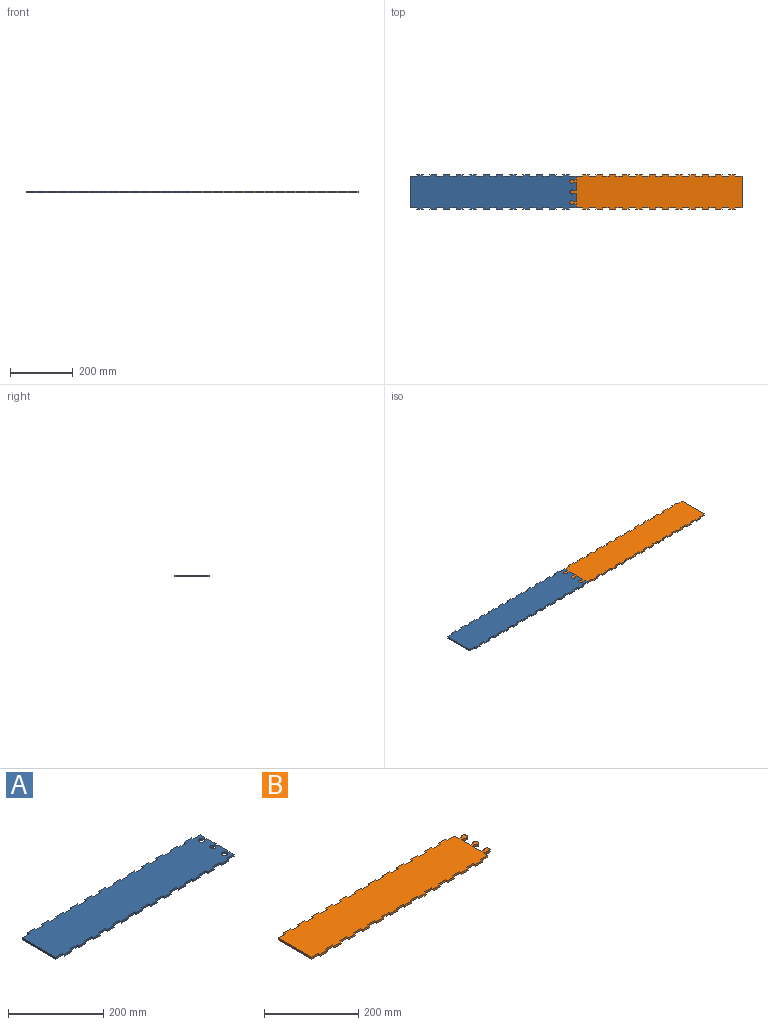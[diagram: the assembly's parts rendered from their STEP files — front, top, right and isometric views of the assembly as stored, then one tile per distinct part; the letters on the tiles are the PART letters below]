
ASSEMBLY  parts=2 mates=1
PART A: 114 faces, bbox 530x110x5.1 mm
  f0: plane 21.2x5.08mm, normal (0,1,0), area 107.7mm2, adj f1,f111,f112,f113
  f1: plane 5.08x5mm, normal (-1,0,0), area 25.4mm2, adj f0,f2,f112,f113
  f2: plane 21.2x5.08mm, normal (0,1,0), area 107.7mm2, adj f1,f3,f112,f113
  f3: plane 5.08x5mm, normal (1,0,0), area 25.4mm2, adj f2,f4,f112,f113
  f4: plane 21.2x5.08mm, normal (0,1,0), area 107.7mm2, adj f3,f5,f112,f113
  f5: plane 5.08x5mm, normal (-1,0,0), area 25.4mm2, adj f4,f6,f112,f113
  f6: plane 21.2x5.08mm, normal (0,1,0), area 107.7mm2, adj f5,f7,f112,f113
  f7: plane 5.08x5mm, normal (1,0,0), area 25.4mm2, adj f6,f8,f112,f113
  f8: plane 21.2x5.08mm, normal (0,1,0), area 107.7mm2, adj f7,f9,f112,f113
  f9: plane 5.08x5mm, normal (-1,0,0), area 25.4mm2, adj f8,f10,f112,f113
  f10: plane 21.2x5.08mm, normal (0,1,0), area 107.7mm2, adj f9,f11,f112,f113
  f11: plane 5.08x5mm, normal (1,0,0), area 25.4mm2, adj f10,f12,f112,f113
  f12: plane 21.2x5.08mm, normal (0,1,0), area 107.7mm2, adj f11,f13,f112,f113
  f13: plane 5.08x5mm, normal (-1,0,0), area 25.4mm2, adj f12,f14,f112,f113
  f14: plane 21.2x5.08mm, normal (0,1,0), area 107.7mm2, adj f13,f15,f112,f113
  f15: plane 5.08x5mm, normal (1,0,0), area 25.4mm2, adj f14,f16,f112,f113
  f16: plane 21.2x5.08mm, normal (0,1,0), area 107.7mm2, adj f15,f17,f112,f113
  f17: plane 5.08x5mm, normal (-1,0,0), area 25.4mm2, adj f16,f18,f112,f113
  f18: plane 21.2x5.08mm, normal (0,1,0), area 107.7mm2, adj f17,f19,f112,f113
  f19: plane 5.08x5mm, normal (1,0,0), area 25.4mm2, adj f18,f20,f112,f113
  f20: plane 21.2x5.08mm, normal (0,1,0), area 107.7mm2, adj f19,f21,f112,f113
  f21: plane 5.08x5mm, normal (-1,0,0), area 25.4mm2, adj f20,f22,f112,f113
  f22: plane 21.2x5.08mm, normal (0,1,0), area 107.7mm2, adj f21,f23,f112,f113
  f23: plane 100x5.08mm, normal (-1,0,0), area 508mm2, adj f22,f24,f112,f113
  f24: plane 21.2x5.08mm, normal (0,-1,0), area 107.7mm2, adj f23,f25,f112,f113
  f25: plane 5.08x5mm, normal (-1,0,0), area 25.4mm2, adj f24,f26,f112,f113
  f26: plane 21.2x5.08mm, normal (0,-1,0), area 107.7mm2, adj f25,f27,f112,f113
  f27: plane 5.08x5mm, normal (1,0,0), area 25.4mm2, adj f26,f28,f112,f113
  f28: plane 21.2x5.08mm, normal (0,-1,0), area 107.7mm2, adj f27,f29,f112,f113
  f29: plane 5.08x5mm, normal (-1,0,0), area 25.4mm2, adj f28,f30,f112,f113
  f30: plane 21.2x5.08mm, normal (0,-1,0), area 107.7mm2, adj f29,f31,f112,f113
  f31: plane 5.08x5mm, normal (1,0,0), area 25.4mm2, adj f30,f32,f112,f113
  f32: plane 21.2x5.08mm, normal (0,-1,0), area 107.7mm2, adj f31,f33,f112,f113
  f33: plane 5.08x5mm, normal (-1,0,0), area 25.4mm2, adj f32,f34,f112,f113
  f34: plane 21.2x5.08mm, normal (0,-1,0), area 107.7mm2, adj f33,f35,f112,f113
  f35: plane 5.08x5mm, normal (1,0,0), area 25.4mm2, adj f34,f36,f112,f113
  f36: plane 21.2x5.08mm, normal (0,-1,0), area 107.7mm2, adj f35,f37,f112,f113
  f37: plane 5.08x5mm, normal (-1,0,0), area 25.4mm2, adj f36,f38,f112,f113
  f38: plane 21.2x5.08mm, normal (0,-1,0), area 107.7mm2, adj f37,f39,f112,f113
  f39: plane 5.08x5mm, normal (1,0,0), area 25.4mm2, adj f38,f40,f112,f113
  f40: plane 21.2x5.08mm, normal (0,-1,0), area 107.7mm2, adj f39,f41,f112,f113
  f41: plane 5.08x5mm, normal (-1,0,0), area 25.4mm2, adj f40,f42,f112,f113
  f42: plane 21.2x5.08mm, normal (0,-1,0), area 107.7mm2, adj f41,f43,f112,f113
  f43: plane 5.08x5mm, normal (1,0,0), area 25.4mm2, adj f42,f44,f112,f113
  f44: plane 21.2x5.08mm, normal (0,-1,0), area 107.7mm2, adj f43,f45,f112,f113
  f45: plane 5.08x5mm, normal (-1,0,0), area 25.4mm2, adj f44,f46,f112,f113
  f46: plane 21.2x5.08mm, normal (0,-1,0), area 107.7mm2, adj f45,f47,f112,f113
  f47: plane 5.08x5mm, normal (1,0,0), area 25.4mm2, adj f46,f48,f112,f113
  f48: plane 21.2x5.08mm, normal (0,-1,0), area 107.7mm2, adj f47,f49,f112,f113
  f49: plane 5.08x5mm, normal (-1,0,0), area 25.4mm2, adj f48,f50,f112,f113
  f50: plane 21.2x5.08mm, normal (0,-1,0), area 107.7mm2, adj f49,f51,f112,f113
  f51: plane 5.08x5mm, normal (1,0,0), area 25.4mm2, adj f50,f52,f112,f113
  f52: plane 21.2x5.08mm, normal (0,-1,0), area 107.7mm2, adj f51,f53,f112,f113
  f53: plane 5.08x5mm, normal (-1,0,0), area 25.4mm2, adj f52,f54,f112,f113
  f54: plane 21.2x5.08mm, normal (0,-1,0), area 107.7mm2, adj f53,f55,f112,f113
  f55: plane 5.08x5mm, normal (1,0,0), area 25.4mm2, adj f54,f56,f112,f113
  f56: plane 21.2x5.08mm, normal (0,-1,0), area 107.7mm2, adj f55,f57,f112,f113
  f57: plane 5.08x5mm, normal (-1,0,0), area 25.4mm2, adj f56,f58,f112,f113
  f58: plane 21.2x5.08mm, normal (0,-1,0), area 107.7mm2, adj f57,f59,f112,f113
  f59: plane 5.08x5mm, normal (1,0,0), area 25.4mm2, adj f58,f60,f112,f113
  f60: plane 21.2x5.08mm, normal (0,-1,0), area 107.7mm2, adj f59,f61,f112,f113
  f61: plane 5.08x5mm, normal (-1,0,0), area 25.4mm2, adj f60,f62,f112,f113
  f62: plane 21.2x5.08mm, normal (0,-1,0), area 107.7mm2, adj f61,f63,f112,f113
  f63: plane 5.08x5mm, normal (1,0,0), area 25.4mm2, adj f62,f64,f112,f113
  f64: plane 21.2x5.08mm, normal (0,-1,0), area 107.7mm2, adj f63,f65,f112,f113
  f65: plane 5.08x5mm, normal (-1,0,0), area 25.4mm2, adj f64,f66,f112,f113
  f66: plane 21.2x5.08mm, normal (0,-1,0), area 107.7mm2, adj f65,f67,f112,f113
  f67: plane 5.08x5mm, normal (1,0,0), area 25.4mm2, adj f66,f68,f112,f113
  f68: plane 21.2x5.08mm, normal (0,-1,0), area 107.7mm2, adj f67,f69,f112,f113
  f69: plane 5.08x5mm, normal (-1,0,0), area 25.4mm2, adj f68,f70,f112,f113
  f70: plane 21.2x5.08mm, normal (0,-1,0), area 107.7mm2, adj f69,f71,f112,f113
  f71: plane 5.08x5mm, normal (1,0,0), area 25.4mm2, adj f70,f72,f112,f113
  f72: plane 21.2x5.08mm, normal (0,-1,0), area 107.7mm2, adj f71,f73,f112,f113
  f73: plane 12.75x5.08mm, normal (1,0,0), area 64.8mm2, adj f72,f74,f112,f113
  f74: plane 7.37x5.08mm, normal (0,1,0), area 37.4mm2, adj f73,f75,f112,f113
  f75: cylinder r=6.5mm len=13mm, axis (0,0,-1), area 172.9mm2, adj f74,f76,f112,f113
  f76: plane 7.37x5.08mm, normal (0,-1,0), area 37.4mm2, adj f75,f77,f112,f113
  f77: plane 27.5x5.08mm, normal (1,0,0), area 139.7mm2, adj f76,f78,f112,f113
  f78: plane 7.37x5.08mm, normal (0,1,0), area 37.4mm2, adj f77,f79,f112,f113
  f79: cylinder r=6.5mm len=13mm, axis (0,0,-1), area 172.9mm2, adj f78,f80,f112,f113
  f80: plane 7.37x5.08mm, normal (0,-1,0), area 37.4mm2, adj f79,f81,f112,f113
  f81: plane 27.5x5.08mm, normal (1,0,0), area 139.7mm2, adj f80,f82,f112,f113
  f82: plane 7.37x5.08mm, normal (0,1,0), area 37.4mm2, adj f81,f83,f112,f113
  f83: cylinder r=6.5mm len=13mm, axis (0,0,-1), area 172.9mm2, adj f82,f84,f112,f113
  f84: plane 7.37x5.08mm, normal (0,-1,0), area 37.4mm2, adj f83,f85,f112,f113
  f85: plane 12.75x5.08mm, normal (1,0,0), area 64.8mm2, adj f84,f86,f112,f113
  f86: plane 21.2x5.08mm, normal (0,1,0), area 107.7mm2, adj f85,f87,f112,f113
  f87: plane 5.08x5mm, normal (1,0,0), area 25.4mm2, adj f86,f88,f112,f113
  f88: plane 21.2x5.08mm, normal (0,1,0), area 107.7mm2, adj f87,f89,f112,f113
  f89: plane 5.08x5mm, normal (-1,0,0), area 25.4mm2, adj f88,f90,f112,f113
  f90: plane 21.2x5.08mm, normal (0,1,0), area 107.7mm2, adj f89,f91,f112,f113
  f91: plane 5.08x5mm, normal (1,0,0), area 25.4mm2, adj f90,f92,f112,f113
  f92: plane 21.2x5.08mm, normal (0,1,0), area 107.7mm2, adj f91,f93,f112,f113
  f93: plane 5.08x5mm, normal (-1,0,0), area 25.4mm2, adj f92,f94,f112,f113
  f94: plane 21.2x5.08mm, normal (0,1,0), area 107.7mm2, adj f93,f95,f112,f113
  f95: plane 5.08x5mm, normal (1,0,0), area 25.4mm2, adj f94,f96,f112,f113
  f96: plane 21.2x5.08mm, normal (0,1,0), area 107.7mm2, adj f95,f97,f112,f113
  f97: plane 5.08x5mm, normal (-1,0,0), area 25.4mm2, adj f96,f98,f112,f113
  f98: plane 21.2x5.08mm, normal (0,1,0), area 107.7mm2, adj f97,f99,f112,f113
  f99: plane 5.08x5mm, normal (1,0,0), area 25.4mm2, adj f98,f100,f112,f113
  f100: plane 21.2x5.08mm, normal (0,1,0), area 107.7mm2, adj f99,f101,f112,f113
  f101: plane 5.08x5mm, normal (-1,0,0), area 25.4mm2, adj f100,f102,f112,f113
  f102: plane 21.2x5.08mm, normal (0,1,0), area 107.7mm2, adj f101,f103,f112,f113
  f103: plane 5.08x5mm, normal (1,0,0), area 25.4mm2, adj f102,f104,f112,f113
  f104: plane 21.2x5.08mm, normal (0,1,0), area 107.7mm2, adj f103,f105,f112,f113
  f105: plane 5.08x5mm, normal (-1,0,0), area 25.4mm2, adj f104,f106,f112,f113
  f106: plane 21.2x5.08mm, normal (0,1,0), area 107.7mm2, adj f105,f107,f112,f113
  f107: plane 5.08x5mm, normal (1,0,0), area 25.4mm2, adj f106,f108,f112,f113
  f108: plane 21.2x5.08mm, normal (0,1,0), area 107.7mm2, adj f107,f109,f112,f113
  f109: plane 5.08x5mm, normal (-1,0,0), area 25.4mm2, adj f108,f110,f112,f113
  f110: plane 21.2x5.08mm, normal (0,1,0), area 107.7mm2, adj f109,f111,f112,f113
  f111: plane 5.08x5mm, normal (1,0,0), area 25.4mm2, adj f0,f110,f112,f113
  f112: plane 530x110mm, normal (0,0,1), area 55013.6mm2, adj f0,f1,f2,f3,f4,f5,f6,f7
  f113: plane 530x110mm, normal (0,0,-1), area 55013.6mm2, adj f0,f1,f2,f3,f4,f5,f6,f7
PART B: 114 faces, bbox 549.5x110x5.1 mm
  f0: plane 21.2x5.08mm, normal (0,1,0), area 107.7mm2, adj f1,f111,f112,f113
  f1: plane 5.08x5mm, normal (-1,0,0), area 25.4mm2, adj f0,f2,f112,f113
  f2: plane 21.2x5.08mm, normal (0,1,0), area 107.7mm2, adj f1,f3,f112,f113
  f3: plane 5.08x5mm, normal (1,0,0), area 25.4mm2, adj f2,f4,f112,f113
  f4: plane 21.2x5.08mm, normal (0,1,0), area 107.7mm2, adj f3,f5,f112,f113
  f5: plane 5.08x5mm, normal (-1,0,0), area 25.4mm2, adj f4,f6,f112,f113
  f6: plane 21.2x5.08mm, normal (0,1,0), area 107.7mm2, adj f5,f7,f112,f113
  f7: plane 100x5.08mm, normal (-1,0,0), area 508mm2, adj f6,f8,f112,f113
  f8: plane 21.2x5.08mm, normal (0,-1,0), area 107.7mm2, adj f7,f9,f112,f113
  f9: plane 5.08x5mm, normal (-1,0,0), area 25.4mm2, adj f8,f10,f112,f113
  f10: plane 21.2x5.08mm, normal (0,-1,0), area 107.7mm2, adj f9,f11,f112,f113
  f11: plane 5.08x5mm, normal (1,0,0), area 25.4mm2, adj f10,f12,f112,f113
  f12: plane 21.2x5.08mm, normal (0,-1,0), area 107.7mm2, adj f11,f13,f112,f113
  f13: plane 5.08x5mm, normal (-1,0,0), area 25.4mm2, adj f12,f14,f112,f113
  f14: plane 21.2x5.08mm, normal (0,-1,0), area 107.7mm2, adj f13,f15,f112,f113
  f15: plane 5.08x5mm, normal (1,0,0), area 25.4mm2, adj f14,f16,f112,f113
  f16: plane 21.2x5.08mm, normal (0,-1,0), area 107.7mm2, adj f15,f17,f112,f113
  f17: plane 5.08x5mm, normal (-1,0,0), area 25.4mm2, adj f16,f18,f112,f113
  f18: plane 21.2x5.08mm, normal (0,-1,0), area 107.7mm2, adj f17,f19,f112,f113
  f19: plane 5.08x5mm, normal (1,0,0), area 25.4mm2, adj f18,f20,f112,f113
  f20: plane 21.2x5.08mm, normal (0,-1,0), area 107.7mm2, adj f19,f21,f112,f113
  f21: plane 5.08x5mm, normal (-1,0,0), area 25.4mm2, adj f20,f22,f112,f113
  f22: plane 21.2x5.08mm, normal (0,-1,0), area 107.7mm2, adj f21,f23,f112,f113
  f23: plane 5.08x5mm, normal (1,0,0), area 25.4mm2, adj f22,f24,f112,f113
  f24: plane 21.2x5.08mm, normal (0,-1,0), area 107.7mm2, adj f23,f25,f112,f113
  f25: plane 5.08x5mm, normal (-1,0,0), area 25.4mm2, adj f24,f26,f112,f113
  f26: plane 21.2x5.08mm, normal (0,-1,0), area 107.7mm2, adj f25,f27,f112,f113
  f27: plane 5.08x5mm, normal (1,0,0), area 25.4mm2, adj f26,f28,f112,f113
  f28: plane 21.2x5.08mm, normal (0,-1,0), area 107.7mm2, adj f27,f29,f112,f113
  f29: plane 5.08x5mm, normal (-1,0,0), area 25.4mm2, adj f28,f30,f112,f113
  f30: plane 21.2x5.08mm, normal (0,-1,0), area 107.7mm2, adj f29,f31,f112,f113
  f31: plane 5.08x5mm, normal (1,0,0), area 25.4mm2, adj f30,f32,f112,f113
  f32: plane 21.2x5.08mm, normal (0,-1,0), area 107.7mm2, adj f31,f33,f112,f113
  f33: plane 5.08x5mm, normal (-1,0,0), area 25.4mm2, adj f32,f34,f112,f113
  f34: plane 21.2x5.08mm, normal (0,-1,0), area 107.7mm2, adj f33,f35,f112,f113
  f35: plane 5.08x5mm, normal (1,0,0), area 25.4mm2, adj f34,f36,f112,f113
  f36: plane 21.2x5.08mm, normal (0,-1,0), area 107.7mm2, adj f35,f37,f112,f113
  f37: plane 5.08x5mm, normal (-1,0,0), area 25.4mm2, adj f36,f38,f112,f113
  f38: plane 21.2x5.08mm, normal (0,-1,0), area 107.7mm2, adj f37,f39,f112,f113
  f39: plane 5.08x5mm, normal (1,0,0), area 25.4mm2, adj f38,f40,f112,f113
  f40: plane 21.2x5.08mm, normal (0,-1,0), area 107.7mm2, adj f39,f41,f112,f113
  f41: plane 5.08x5mm, normal (-1,0,0), area 25.4mm2, adj f40,f42,f112,f113
  f42: plane 21.2x5.08mm, normal (0,-1,0), area 107.7mm2, adj f41,f43,f112,f113
  f43: plane 5.08x5mm, normal (1,0,0), area 25.4mm2, adj f42,f44,f112,f113
  f44: plane 21.2x5.08mm, normal (0,-1,0), area 107.7mm2, adj f43,f45,f112,f113
  f45: plane 5.08x5mm, normal (-1,0,0), area 25.4mm2, adj f44,f46,f112,f113
  f46: plane 21.2x5.08mm, normal (0,-1,0), area 107.7mm2, adj f45,f47,f112,f113
  f47: plane 5.08x5mm, normal (1,0,0), area 25.4mm2, adj f46,f48,f112,f113
  f48: plane 21.2x5.08mm, normal (0,-1,0), area 107.7mm2, adj f47,f49,f112,f113
  f49: plane 5.08x5mm, normal (-1,0,0), area 25.4mm2, adj f48,f50,f112,f113
  f50: plane 21.2x5.08mm, normal (0,-1,0), area 107.7mm2, adj f49,f51,f112,f113
  f51: plane 5.08x5mm, normal (1,0,0), area 25.4mm2, adj f50,f52,f112,f113
  f52: plane 21.2x5.08mm, normal (0,-1,0), area 107.7mm2, adj f51,f53,f112,f113
  f53: plane 5.08x5mm, normal (-1,0,0), area 25.4mm2, adj f52,f54,f112,f113
  f54: plane 21.2x5.08mm, normal (0,-1,0), area 107.7mm2, adj f53,f55,f112,f113
  f55: plane 5.08x5mm, normal (1,0,0), area 25.4mm2, adj f54,f56,f112,f113
  f56: plane 21.2x5.08mm, normal (0,-1,0), area 107.7mm2, adj f55,f57,f112,f113
  f57: plane 12.75x5.08mm, normal (1,0,0), area 64.8mm2, adj f56,f58,f112,f113
  f58: plane 7.37x5.08mm, normal (0,-1,0), area 37.4mm2, adj f57,f59,f112,f113
  f59: cylinder r=6.5mm len=13mm, axis (0,0,-1), area 172.9mm2, adj f58,f60,f112,f113
  f60: plane 7.37x5.08mm, normal (0,1,0), area 37.4mm2, adj f59,f61,f112,f113
  f61: plane 27.5x5.08mm, normal (1,0,0), area 139.7mm2, adj f60,f62,f112,f113
  f62: plane 7.37x5.08mm, normal (0,-1,0), area 37.4mm2, adj f61,f63,f112,f113
  f63: cylinder r=6.5mm len=13mm, axis (0,0,-1), area 172.9mm2, adj f62,f64,f112,f113
  f64: plane 7.37x5.08mm, normal (0,1,0), area 37.4mm2, adj f63,f65,f112,f113
  f65: plane 27.5x5.08mm, normal (1,0,0), area 139.7mm2, adj f64,f66,f112,f113
  f66: plane 7.37x5.08mm, normal (0,-1,0), area 37.4mm2, adj f65,f67,f112,f113
  f67: cylinder r=6.5mm len=13mm, axis (0,0,-1), area 172.9mm2, adj f66,f68,f112,f113
  f68: plane 7.37x5.08mm, normal (0,1,0), area 37.4mm2, adj f67,f69,f112,f113
  f69: plane 12.75x5.08mm, normal (1,0,0), area 64.8mm2, adj f68,f70,f112,f113
  f70: plane 21.2x5.08mm, normal (0,1,0), area 107.7mm2, adj f69,f71,f112,f113
  f71: plane 5.08x5mm, normal (1,0,0), area 25.4mm2, adj f70,f72,f112,f113
  f72: plane 21.2x5.08mm, normal (0,1,0), area 107.7mm2, adj f71,f73,f112,f113
  f73: plane 5.08x5mm, normal (-1,0,0), area 25.4mm2, adj f72,f74,f112,f113
  f74: plane 21.2x5.08mm, normal (0,1,0), area 107.7mm2, adj f73,f75,f112,f113
  f75: plane 5.08x5mm, normal (1,0,0), area 25.4mm2, adj f74,f76,f112,f113
  f76: plane 21.2x5.08mm, normal (0,1,0), area 107.7mm2, adj f75,f77,f112,f113
  f77: plane 5.08x5mm, normal (-1,0,0), area 25.4mm2, adj f76,f78,f112,f113
  f78: plane 21.2x5.08mm, normal (0,1,0), area 107.7mm2, adj f77,f79,f112,f113
  f79: plane 5.08x5mm, normal (1,0,0), area 25.4mm2, adj f78,f80,f112,f113
  f80: plane 21.2x5.08mm, normal (0,1,0), area 107.7mm2, adj f79,f81,f112,f113
  f81: plane 5.08x5mm, normal (-1,0,0), area 25.4mm2, adj f80,f82,f112,f113
  f82: plane 21.2x5.08mm, normal (0,1,0), area 107.7mm2, adj f81,f83,f112,f113
  f83: plane 5.08x5mm, normal (1,0,0), area 25.4mm2, adj f82,f84,f112,f113
  f84: plane 21.2x5.08mm, normal (0,1,0), area 107.7mm2, adj f83,f85,f112,f113
  f85: plane 5.08x5mm, normal (-1,0,0), area 25.4mm2, adj f84,f86,f112,f113
  f86: plane 21.2x5.08mm, normal (0,1,0), area 107.7mm2, adj f85,f87,f112,f113
  f87: plane 5.08x5mm, normal (1,0,0), area 25.4mm2, adj f86,f88,f112,f113
  f88: plane 21.2x5.08mm, normal (0,1,0), area 107.7mm2, adj f87,f89,f112,f113
  f89: plane 5.08x5mm, normal (-1,0,0), area 25.4mm2, adj f88,f90,f112,f113
  f90: plane 21.2x5.08mm, normal (0,1,0), area 107.7mm2, adj f89,f91,f112,f113
  f91: plane 5.08x5mm, normal (1,0,0), area 25.4mm2, adj f90,f92,f112,f113
  f92: plane 21.2x5.08mm, normal (0,1,0), area 107.7mm2, adj f91,f93,f112,f113
  f93: plane 5.08x5mm, normal (-1,0,0), area 25.4mm2, adj f92,f94,f112,f113
  f94: plane 21.2x5.08mm, normal (0,1,0), area 107.7mm2, adj f93,f95,f112,f113
  f95: plane 5.08x5mm, normal (1,0,0), area 25.4mm2, adj f94,f96,f112,f113
  f96: plane 21.2x5.08mm, normal (0,1,0), area 107.7mm2, adj f95,f97,f112,f113
  f97: plane 5.08x5mm, normal (-1,0,0), area 25.4mm2, adj f96,f98,f112,f113
  f98: plane 21.2x5.08mm, normal (0,1,0), area 107.7mm2, adj f97,f99,f112,f113
  f99: plane 5.08x5mm, normal (1,0,0), area 25.4mm2, adj f98,f100,f112,f113
  f100: plane 21.2x5.08mm, normal (0,1,0), area 107.7mm2, adj f99,f101,f112,f113
  f101: plane 5.08x5mm, normal (-1,0,0), area 25.4mm2, adj f100,f102,f112,f113
  f102: plane 21.2x5.08mm, normal (0,1,0), area 107.7mm2, adj f101,f103,f112,f113
  f103: plane 5.08x5mm, normal (1,0,0), area 25.4mm2, adj f102,f104,f112,f113
  f104: plane 21.2x5.08mm, normal (0,1,0), area 107.7mm2, adj f103,f105,f112,f113
  f105: plane 5.08x5mm, normal (-1,0,0), area 25.4mm2, adj f104,f106,f112,f113
  f106: plane 21.2x5.08mm, normal (0,1,0), area 107.7mm2, adj f105,f107,f112,f113
  f107: plane 5.08x5mm, normal (1,0,0), area 25.4mm2, adj f106,f108,f112,f113
  f108: plane 21.2x5.08mm, normal (0,1,0), area 107.7mm2, adj f107,f109,f112,f113
  f109: plane 5.08x5mm, normal (-1,0,0), area 25.4mm2, adj f108,f110,f112,f113
  f110: plane 21.2x5.08mm, normal (0,1,0), area 107.7mm2, adj f109,f111,f112,f113
  f111: plane 5.08x5mm, normal (1,0,0), area 25.4mm2, adj f0,f110,f112,f113
  f112: plane 549.5x110mm, normal (0,0,1), area 56074.4mm2, adj f0,f1,f2,f3,f4,f5,f6,f7
  f113: plane 549.5x110mm, normal (0,0,-1), area 56074.4mm2, adj f0,f1,f2,f3,f4,f5,f6,f7
PLACE A t=(-67.88,112.37,-79.69)mm fixed
PLACE B rot(axis=(0,0,1),180deg) t=(992.12,12.37,-79.69)mm
MATE planar A.f84 <-> B.f58  axis (0,-1,0) through (458.43,99.62,-77.15)mm
